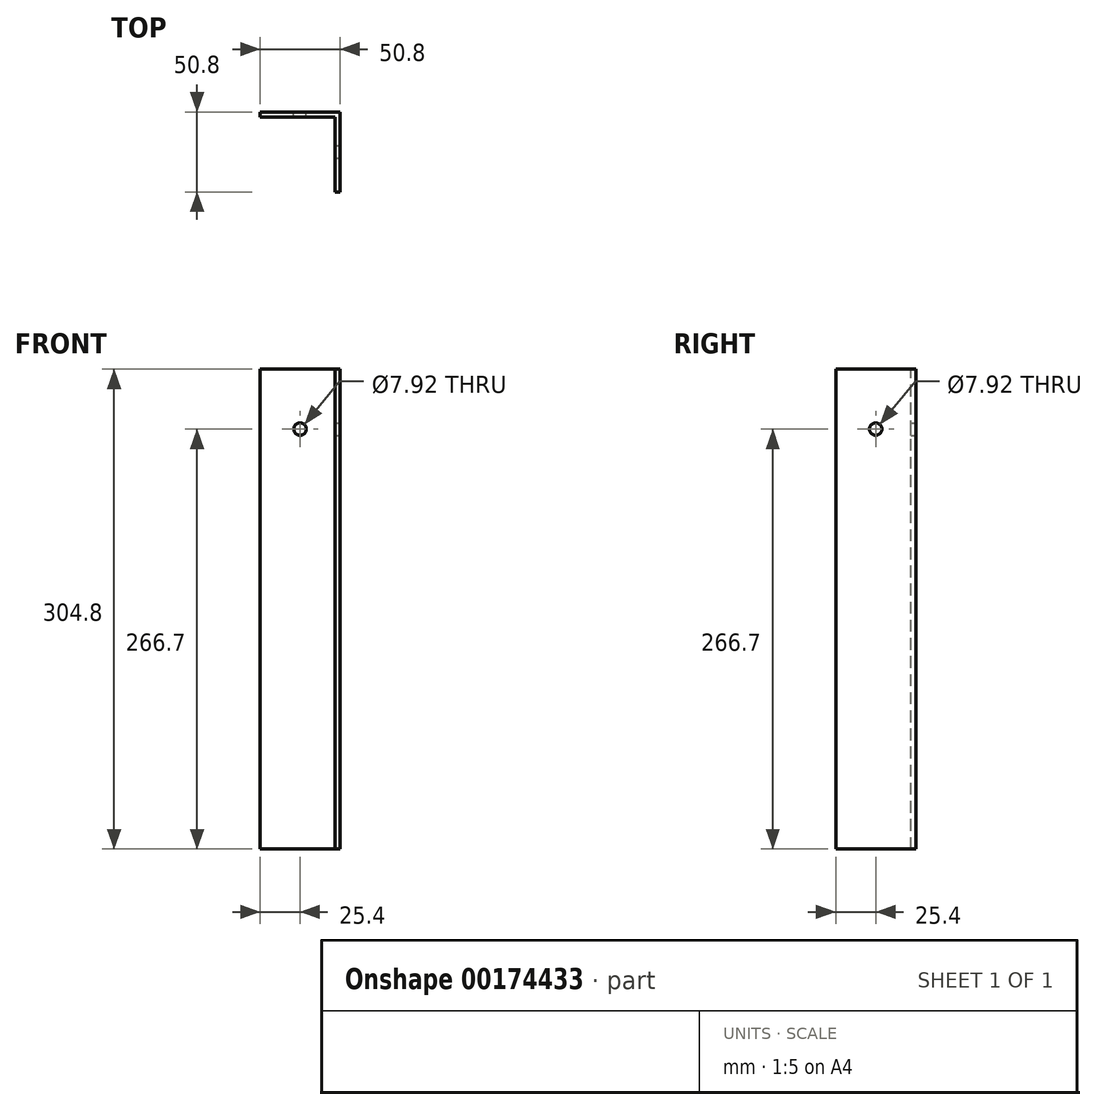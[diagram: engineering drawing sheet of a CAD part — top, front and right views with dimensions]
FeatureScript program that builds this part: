
annotation { "Feature Type Name" : "Feature", "Feature Type Description" : "" }
export const myFeature = defineFeature(function(context is Context, id is Id, definition is map)
    precondition{}
    {
        {
            var Q0;
            Q0=qCreatedBy(makeId("Top.planeOp"),FACE);
            var sketch = newSketch(context, id + "F0", { "sketchPlane" : qUnion([Q0])});
            skLineSegment(sketch, "E0", {"start": v(-50.8, 0) * mm, "end": v(0, 0) * mm});
            skLineSegment(sketch, "E1", {"start": v(0, 0) * mm, "end": v(0, -50.8) * mm});
            skLineSegment(sketch, "E2", {"start": v(-50.8, 0) * mm, "end": v(-50.8, -3.18) * mm});
            skLineSegment(sketch, "E3", {"start": v(-50.8, -3.18) * mm, "end": v(-3.18, -3.18) * mm});
            skLineSegment(sketch, "E4", {"start": v(-3.18, -3.18) * mm, "end": v(-3.17, -50.8) * mm});
            skLineSegment(sketch, "E5", {"start": v(0, -50.8) * mm, "end": v(-3.17, -50.8) * mm});
            skSolve(sketch);
        }
        {
            var Q0;
            Q0 = qSketchRegion(id + "F0", true);
            extrude(context, id + "F1", {"entities" : qUnion([Q0]), "oppositeDirection" : true, "depth" : 304.8 * mm});
        }
        {
            var Q0;
            Q0=qCreatedBy(makeId("Right.planeOp"),FACE);
            var sketch = newSketch(context, id + "F2", { "sketchPlane" : qUnion([Q0])});
            skCircle(sketch, "E6", {"center": v(-25.4, -38.1) * mm, "radius": 3.96 * mm});
            skSolve(sketch);
        }
        {
            var Q0;
            Q0=makeQuery(id+"F2.imprint","IMPRINT",FACE,{"disambiguationData":[TD([[makeQuery(id+"F2.imprint","IMPRINT",EDGE,{"derivedFrom":sQuery(id+"F2.wireOp",EDGE,"E6")}),1.0]])]});
            extrude(context, id + "F3", {"entities" : qUnion([Q0]), "operationType" : NewBodyOperationType.REMOVE, "endBound" : BoundingType.THROUGH_ALL, "oppositeDirection" : true, "depth" : 25.4 * mm});
        }
        {
            var Q0;
            Q0=qCreatedBy(makeId("Front.planeOp"),FACE);
            var sketch = newSketch(context, id + "F4", { "sketchPlane" : qUnion([Q0])});
            skCircle(sketch, "E7", {"center": v(-25.4, -38.1) * mm, "radius": 3.96 * mm});
            skSolve(sketch);
        }
        {
            var Q0;
            Q0=makeQuery(id+"F4.imprint","IMPRINT",FACE,{"disambiguationData":[TD([[makeQuery(id+"F4.imprint","IMPRINT",EDGE,{"derivedFrom":sQuery(id+"F4.wireOp",EDGE,"E7")}),1.0]])]});
            extrude(context, id + "F5", {"entities" : qUnion([Q0]), "operationType" : NewBodyOperationType.REMOVE, "endBound" : BoundingType.THROUGH_ALL, "depth" : 25.4 * mm});
        }
    });
